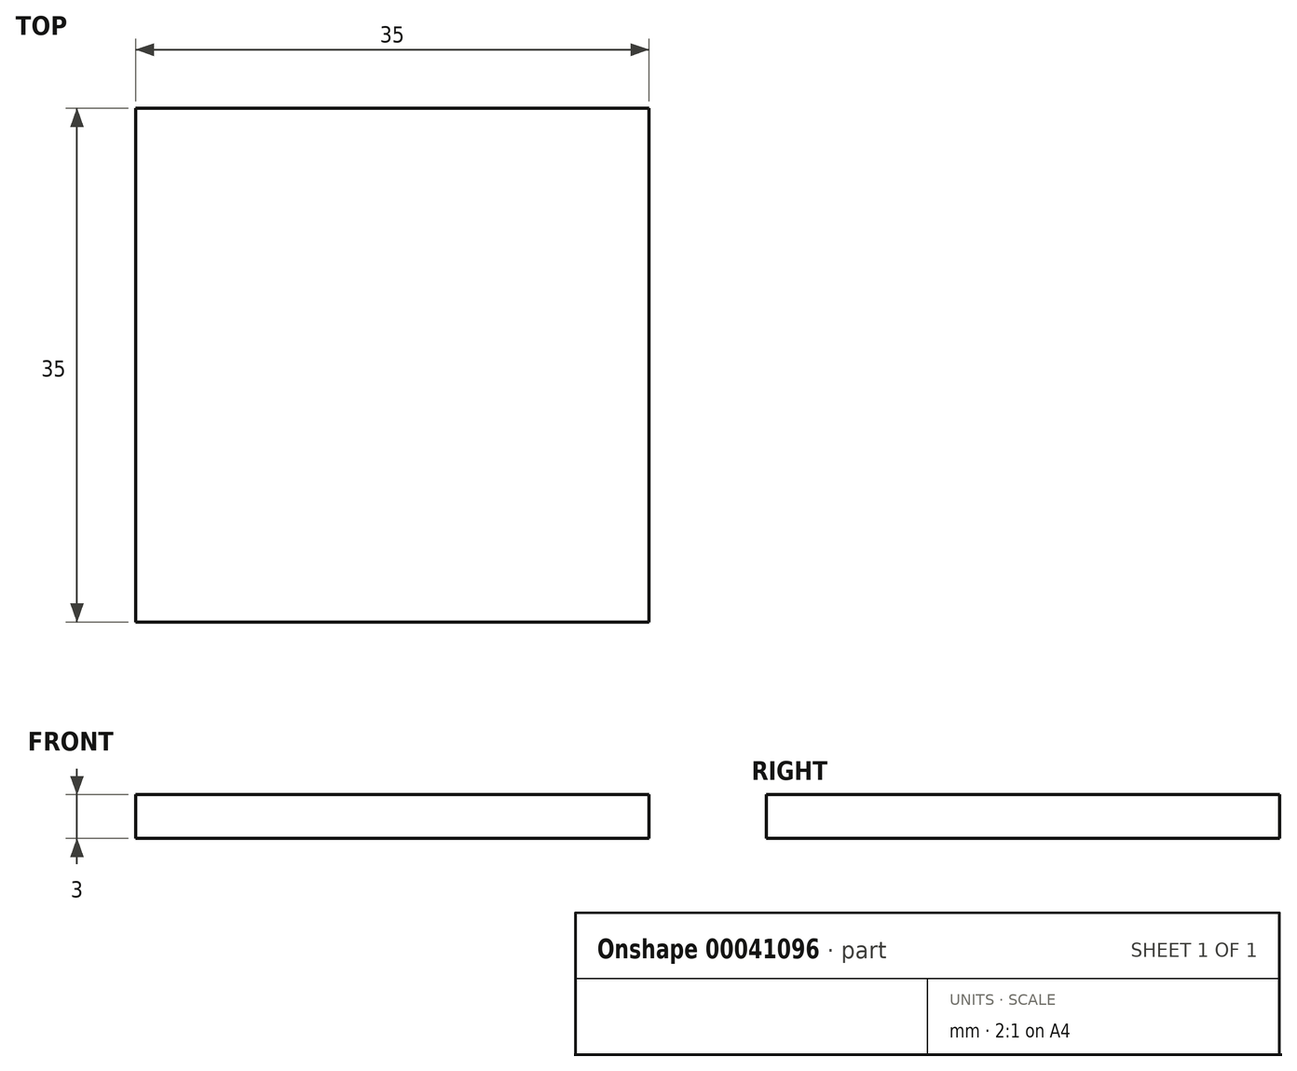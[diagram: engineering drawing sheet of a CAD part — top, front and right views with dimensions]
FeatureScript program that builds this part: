
annotation { "Feature Type Name" : "Feature", "Feature Type Description" : "" }
export const myFeature = defineFeature(function(context is Context, id is Id, definition is map)
    precondition{}
    {
        {
            var Q0;
            Q0=qCreatedBy(makeId("Top.planeOp"),FACE);
            var sketch = newSketch(context, id + "F0", { "sketchPlane" : qUnion([Q0])});
            skLineSegment(sketch, "E0.bottom", {"start": v(0, 0) * mm, "end": v(35, 0) * mm});
            skLineSegment(sketch, "E0.top", {"start": v(0, 35) * mm, "end": v(35, 35) * mm});
            skLineSegment(sketch, "E0.left", {"start": v(0, 0) * mm, "end": v(0, 35) * mm});
            skLineSegment(sketch, "E0.right", {"start": v(35, 0) * mm, "end": v(35, 35) * mm});
            skSolve(sketch);
        }
        {
            var Q0;
            Q0 = qSketchRegion(id + "F0", true);
            extrude(context, id + "F1", {"entities" : qUnion([Q0]), "depth" : 3 * mm});
        }
    });
